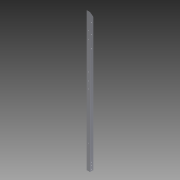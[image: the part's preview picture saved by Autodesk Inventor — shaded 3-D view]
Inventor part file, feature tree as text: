
AUTODESK INVENTOR PART (.ipt)
format: ipt  version: 2015 (Build 190159000, 159)  size: 179,200 bytes
history: native  units: in
note: dims shown in document units (in); Inventor stores cm internally (conversion verified against a paired STEP export)
features: sketch x7, hole x5, projected_geometry x3, extrude x2
ambient origin geometry x8: Origin, YZ Plane, XZ Plane, XY Plane, X Axis, Y Axis, Z Axis, Center Point
bodies: Solid1 (feature_tree)
feature tree (17):
  extrude  "Extrusion1"  Depth=1.0in
  hole  "Hole1"  [1 undecoded]
  extrude  "Extrusion2"  Depth=0.125in
  hole  "Hole5"  [1 undecoded]
  hole  "Hole6"  [1 undecoded]
  hole  "Hole10"  [1 undecoded]
  hole  "Hole11"  [1 undecoded]
  sketch  "Sketch1"  dims[d0=1.0in d1=1.0in]
  sketch  "Sketch2"  dims[d2=0.75in d3=0.75in]
  projected_geometry  "Projected Loop1"
  sketch  "Sketch3"  dims[d4=0.125in d5=0.125in]
  projected_geometry  "Projected Loop2"
  sketch  "Sketch5"  dims[d6=39.875in d7=0.0in d8=0.5in]
  sketch  "Sketch6"  dims[d9=1.5in d14=0.5in]
  sketch  "Sketch10"  dims[d15=0.5in]
  sketch  "Sketch11"  dims[d16=0.25in d17=0.75in d18=0.375in d19=0.25in d20=0.5635in d21=1.0in d22=0.8108in d26=1.0in d27=0.0in d57=60.0deg d58=0.5in d59=30.5in d60=0.25in d61=0.75in d62=0.375in d63=0.25in d64=0.5635in d65=1.0in d66=0.8108in d67=0.5in d68=0.5in d69=34.0in d70=37.0in d71=0.25in d72=0.75in d73=0.375in d74=0.25in d75=0.5635in d76=1.0in d77=0.8108in d114=0.5in d115=0.5in d116=35.0in d117=32.75in d118=22.5in d119=24.75in d120=0.5in d121=0.5in d122=0.5in d123=20.5in d124=7.0in d125=0.5in d126=0.25in d127=0.75in d128=0.375in d129=0.25in d130=0.5635in d131=1.0in d132=0.8108in d133=2.25in d134=0.5in d135=0.25in d136=0.75in d137=0.375in d138=0.25in d139=0.5635in d140=1.0in d141=0.8108in]
  projected_geometry  "Projected Loop5"
note: 5 required parameter values undecoded (feature->parameter linkage not recoverable at this tier; creation-order binding heuristic only, values carry confidence <= 0.55)
